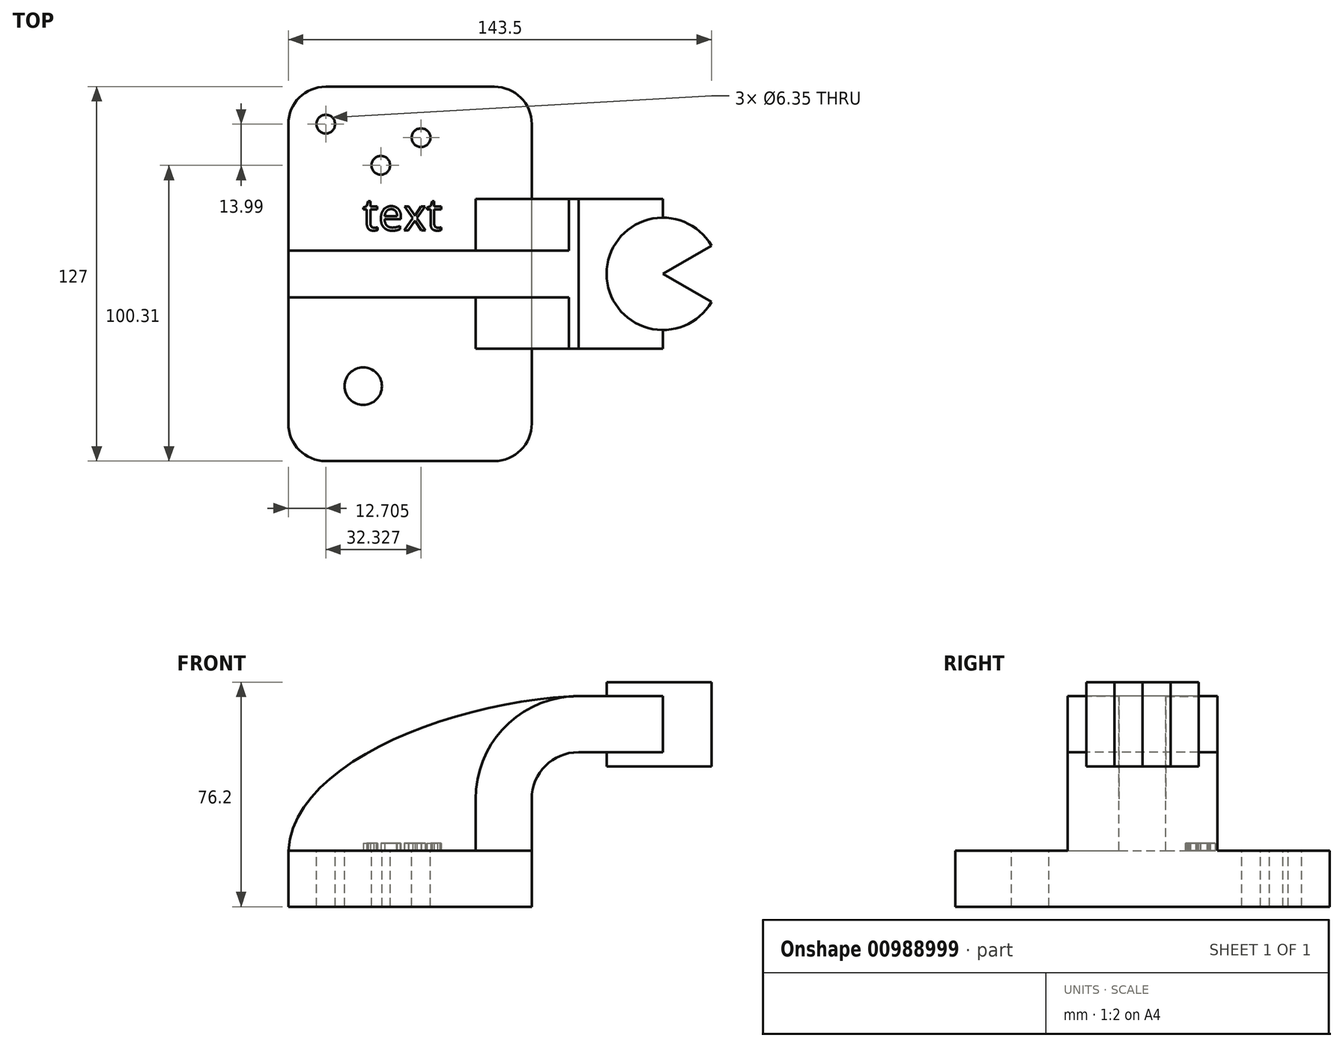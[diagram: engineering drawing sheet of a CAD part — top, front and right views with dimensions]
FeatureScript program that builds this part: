
annotation { "Feature Type Name" : "Feature", "Feature Type Description" : "" }
export const myFeature = defineFeature(function(context is Context, id is Id, definition is map)
    precondition{}
    {
        {
            var Q0;
            Q0=qCreatedBy(makeId("Front.planeOp"),FACE);
            var sketch = newSketch(context, id + "F0", { "sketchPlane" : qUnion([Q0])});
            skLineSegment(sketch, "E0.rect.bottom", {"start": v(-41.28, 9.53) * mm, "end": v(41.28, 9.53) * mm});
            skLineSegment(sketch, "E0.rect.top", {"start": v(-41.28, -9.52) * mm, "end": v(41.28, -9.52) * mm});
            skLineSegment(sketch, "E0.rect.left", {"start": v(-41.28, 9.52) * mm, "end": v(-41.28, -9.52) * mm});
            skLineSegment(sketch, "E0.rect.right", {"start": v(41.28, 9.52) * mm, "end": v(41.28, -9.52) * mm});
            skPoint(sketch, "E0.rect.middle", {"position": v(0, 0) * mm});
            skLineSegment(sketch, "E1", {"start": v(41.28, 9.52) * mm, "end": v(41.28, 27) * mm});
            skArc(sketch, "E2", {"start": v(41.28, 27) * mm, "mid": v(45.92, 38.23) * mm, "end": v(57.15, 42.88) * mm});
            skLineSegment(sketch, "E3", {"start": v(57.15, 42.88) * mm, "end": v(85.72, 42.88) * mm});
            skLineSegment(sketch, "E4.rect.bottom", {"start": v(66.67, 38.1) * mm, "end": v(104.78, 38.1) * mm});
            skLineSegment(sketch, "E4.rect.top", {"start": v(66.67, 66.68) * mm, "end": v(104.77, 66.68) * mm});
            skLineSegment(sketch, "E4.rect.left", {"start": v(66.67, 38.1) * mm, "end": v(66.67, 66.67) * mm});
            skLineSegment(sketch, "E4.rect.right", {"start": v(104.77, 38.1) * mm, "end": v(104.77, 66.68) * mm});
            skPoint(sketch, "E4.rect.middle", {"position": v(85.72, 52.39) * mm});
            skLineSegment(sketch, "E5.0", {"start": v(57.15, 61.93) * mm, "end": v(85.72, 61.93) * mm});
            skArc(sketch, "E5.1", {"start": v(22.23, 27) * mm, "mid": v(32.45, 51.7) * mm, "end": v(57.15, 61.93) * mm});
            skLineSegment(sketch, "E5.2", {"start": v(22.23, 9.52) * mm, "end": v(22.23, 27) * mm});
            skLineSegment(sketch, "E6", {"start": v(85.72, 38.1) * mm, "end": v(85.72, 66.68) * mm});
            skFitSpline(sketch, "E7", {"points": [v(-41.28, 9.53) * mm, v(57.15, 61.93) * mm], "startDerivative": vector(5.2, 92.34) * mm, "endDerivative": vector(120.92, 4.22) * mm});
            skSolve(sketch);
        }
        {
            var Q0;
            Q0=makeQuery(id+"F0.imprint","IMPRINT",FACE,{"disambiguationData":[TD([[makeQuery(id+"F0.imprint","IMPRINT",EDGE,{"derivedFrom":sQuery(id+"F0.wireOp",EDGE,"E0.rect.top")}),1.0]])]});
            extrude(context, id + "F1", {"entities" : qUnion([Q0]), "endBound" : BoundingType.SYMMETRIC, "offsetDistance" : 25.4 * mm, "depth" : 127 * mm});
        }
        {
            var Q0;
            {var subQ9=sQuery(id+"F0.wireOp",EDGE,"E1");Q0=makeQuery(id+"F0.imprint","IMPRINT",FACE,{"disambiguationData":[TD([[makeQuery(id+"F0.imprint","IMPRINT",EDGE,{"derivedFrom":subQ9}),1.0]])]});}
            var Q1;
            {var subQ0=sQuery(id+"F0.wireOp",EDGE,"E6");var subQ1=sQuery(id+"F0.wireOp",EDGE,"E3");var subQ2=makeQuery(id+"F0.imprint","INTERSECT",VERTEX,{"derivedFrom":[subQ1,subQ0]});Q1=makeQuery(id+"F0.imprint","IMPRINT",FACE,{"disambiguationData":[TD([[makeQuery(id+"F0.imprint","IMPRINT",EDGE,{"disambiguationData":[TD([[subQ2,1.0]])],"derivedFrom":subQ1}),1.0]])]});}
            extrude(context, id + "F2", {"entities" : qUnion([Q0, Q1]), "operationType" : NewBodyOperationType.ADD, "endBound" : BoundingType.SYMMETRIC, "depth" : 50.8 * mm});
        }
        {
            var Q0;
            {var subQ3=sQuery(id+"F0.wireOp",EDGE,"E5.2");Q0=makeQuery(id+"F0.imprint","IMPRINT",FACE,{"disambiguationData":[TD([[makeQuery(id+"F0.imprint","IMPRINT",EDGE,{"derivedFrom":subQ3}),1.0]])]});}
            extrude(context, id + "F3", {"entities" : qUnion([Q0]), "operationType" : NewBodyOperationType.ADD, "endBound" : BoundingType.SYMMETRIC, "depth" : 15.88 * mm});
        }
        {
            var Q0;
            {var subQ5=sQuery(id+"F0.wireOp",EDGE,"E4.rect.right");Q0=makeQuery(id+"F0.imprint","IMPRINT",FACE,{"disambiguationData":[TD([[makeQuery(id+"F0.imprint","IMPRINT",EDGE,{"derivedFrom":subQ5}),1.0]])]});}
            var Q1;
            Q1=sQuery(id+"F0.wireOp",EDGE,"E6");
            revolve(context, id + "F4", {"operationType" : NewBodyOperationType.ADD, "surfaceOperationType" : NewSurfaceOperationType.NEW, "entities" : qUnion([Q0]), "axis" : qUnion([Q1]), "revolveType" : RevolveType.TWO_DIRECTIONS, "angle" : 330 * degree, "angleBack" : 30 * degree});
        }
        {
            var Q0;
            Q0=makeQuery(id+"F1.opExtrude","CAP_EDGE",EDGE,{"disambiguationData":[OSD([sQuery(id+"F0.wireOp",EDGE,"E0.rect.right")])],"isStart":false});
            var Q1;
            Q1=makeQuery(id+"F1.opExtrude","CAP_EDGE",EDGE,{"disambiguationData":[OSD([sQuery(id+"F0.wireOp",EDGE,"E0.rect.left")])],"isStart":false});
            var Q2;
            Q2=makeQuery(id+"F1.opExtrude","CAP_EDGE",EDGE,{"disambiguationData":[OSD([sQuery(id+"F0.wireOp",EDGE,"E0.rect.right")])],"isStart":true});
            var Q3;
            Q3=makeQuery(id+"F1.opExtrude","CAP_EDGE",EDGE,{"disambiguationData":[OSD([sQuery(id+"F0.wireOp",EDGE,"E0.rect.left")])],"isStart":true});
            fillet(context, id + "F5", {"entities" : qUnion([Q0, Q1, Q2, Q3]), "radius" : 12.7 * mm, "tangentPropagation" : true, "allowEdgeOverflow" : false});
        }
        {
            var Q0;
            {var subQ4=sQuery(id+"F0.wireOp",EDGE,"E0.rect.bottom");var subQ5=sQuery(id+"F0.wireOp",EDGE,"E0.rect.right");var subQ6=sQuery(id+"F0.wireOp",EDGE,"E0.rect.left");Q0=makeQuery(id+"F3.boolean.opBoolean","SPLIT",FACE,{"disambiguationData":[TD([makeQuery(id+"F1.opExtrude","CAP_FACE",FACE,{"disambiguationData":[OSD([subQ4,sQuery(id+"F0.wireOp",EDGE,"E0.rect.top"),subQ6,subQ5])],"isStart":false})])],"derivedFrom":makeQuery(id+"F1.opExtrude","SWEPT_FACE",FACE,{"disambiguationData":[OSD([subQ4])]})});}
            var sketch = newSketch(context, id + "F6", { "sketchPlane" : qUnion([Q0])});
            skCircle(sketch, "E8", {"center": v(-15.88, -38.1) * mm, "radius": 6.35 * mm});
            skSolve(sketch);
        }
        {
            var Q0;
            Q0=makeQuery(id+"F6.imprint","IMPRINT",FACE,{"disambiguationData":[TD([[makeQuery(id+"F6.imprint","IMPRINT",EDGE,{"derivedFrom":sQuery(id+"F6.wireOp",EDGE,"E8")}),1.0]])]});
            extrude(context, id + "F7", {"entities" : qUnion([Q0]), "operationType" : NewBodyOperationType.REMOVE, "endBound" : BoundingType.UP_TO_NEXT, "oppositeDirection" : true, "depth" : 25.4 * mm, "offsetDistance" : 25.4 * mm});
        }
        {
            var Q0;
            {var subQ4=sQuery(id+"F0.wireOp",EDGE,"E0.rect.bottom");var subQ5=sQuery(id+"F0.wireOp",EDGE,"E0.rect.right");var subQ6=sQuery(id+"F0.wireOp",EDGE,"E0.rect.left");Q0=makeQuery(id+"F3.boolean.opBoolean","SPLIT",FACE,{"disambiguationData":[TD([makeQuery(id+"F1.opExtrude","CAP_FACE",FACE,{"disambiguationData":[OSD([subQ4,sQuery(id+"F0.wireOp",EDGE,"E0.rect.top"),subQ6,subQ5])],"isStart":true})])],"derivedFrom":makeQuery(id+"F1.opExtrude","SWEPT_FACE",FACE,{"disambiguationData":[OSD([subQ4])]})});}
            var sketch = newSketch(context, id + "F8", { "sketchPlane" : qUnion([Q0])});
            skPoint(sketch, "E9", {"position": v(3.75, 46.19) * mm});
            skPoint(sketch, "E10", {"position": v(-9.9, 36.8) * mm});
            skPoint(sketch, "E11", {"position": v(-28.58, 50.8) * mm});
            skSolve(sketch);
        }
        {
            var Q0;
            Q0=sQuery(id+"F8.wireOp",VERTEX,"E10");
            var Q1;
            Q1=sQuery(id+"F8.wireOp",VERTEX,"E9");
            var Q2;
            Q2=sQuery(id+"F8.wireOp",VERTEX,"E11");
            var Q3;
            Q3=makeQuery(id+"F1.opExtrude","SWEPT_BODY",BODY,{"disambiguationData":[OSD([sQuery(id+"F0.wireOp",EDGE,"E0.rect.bottom"),sQuery(id+"F0.wireOp",EDGE,"E0.rect.top"),sQuery(id+"F0.wireOp",EDGE,"E0.rect.left"),sQuery(id+"F0.wireOp",EDGE,"E0.rect.right")])]});
            hole(context, id + "F9", {"style" : HoleStyle.SIMPLE, "endStyle" : HoleEndStyle.THROUGH, "holeDiameter" : 6.35 * mm, "majorDiameter" : 6.35 * mm, "isTappedThrough" : true, "tappedDepth" : 12.7 * mm, "tapClearance" : 3, "locations" : qUnion([Q0, Q1, Q2]), "scope" : qUnion([Q3])});
        }
        {
            var Q0;
            {var subQ4=sQuery(id+"F0.wireOp",EDGE,"E0.rect.bottom");var subQ5=sQuery(id+"F0.wireOp",EDGE,"E0.rect.right");var subQ6=sQuery(id+"F0.wireOp",EDGE,"E0.rect.left");Q0=makeQuery(id+"F3.boolean.opBoolean","SPLIT",FACE,{"disambiguationData":[TD([makeQuery(id+"F1.opExtrude","CAP_FACE",FACE,{"disambiguationData":[OSD([subQ4,sQuery(id+"F0.wireOp",EDGE,"E0.rect.top"),subQ6,subQ5])],"isStart":false})])],"derivedFrom":makeQuery(id+"F1.opExtrude","SWEPT_FACE",FACE,{"disambiguationData":[OSD([subQ4])]})});}
            var sketch = newSketch(context, id + "F10", { "sketchPlane" : qUnion([Q0])});
            skText(sketch, "E12", { "text": "text", "fontName": "OpenSans-Regular.ttf"});
            const initialGuessF10  = {"E12": [-0.01603, 0.01477, 1, 0, 0.01083]};
            skSetInitialGuess(sketch, initialGuessF10);
            skSolve(sketch);
        }
        {
            var Q0;
            Q0 = qSketchRegion(id + "F10", true);
            extrude(context, id + "F11", {"entities" : qUnion([Q0]), "operationType" : NewBodyOperationType.ADD, "depth" : 2.54 * mm, "offsetDistance" : 25.4 * mm});
        }
    });
